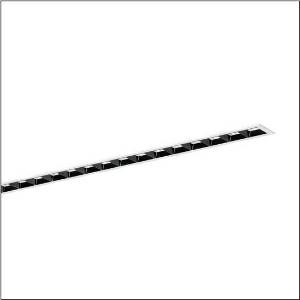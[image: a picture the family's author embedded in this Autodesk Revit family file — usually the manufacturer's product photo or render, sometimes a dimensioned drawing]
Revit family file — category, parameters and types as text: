
# Revit family: silica_r__21_51mx12tbt5w_1d14
name_source: partatom
category: Lighting Fixtures
units: mm (PartAtom-declared; Revit-internal decimal feet)

## family parameters
Cut with Voids When Loaded = No
Host = Face
Light Source = No
Part Type = Normal
Room Calculation Point = No
Round Connector Dimension = Use Diameter
Shared = No

## types (1)
- --- (1 x LED, 4650 lm, 40.2 W, 6500K)
    Apparent Load = 40 VA
    CIE Flux Codes = 84 100 100 100 100
    Color Rendering = 80
    Color Temperature = 6500K
    Default Elevation = 1800 mm
    Description = Silica® 21, office luminaire, primary light control with darklight reflector, of PMMA, black, CAT 2 (L<= 3000cd/m²), light emission: direct distribution, primary light characteristic: symmetric, installation type: recessed, LED, rated luminous flux: 4.650lm, luminous efficacy: 110lm/W, light colour: 8tw, colour temperature: 2700..6500K, with terminal, 3+2-pole, max. 2.5mm², mains connection: 220..240V, AC, 50/60Hz, rated input power: 42.2W, luminaire housing, of aluminium, traffic white (RAL 9016), length: 1.528mm, width: 79mm, height: 53mm, protection rating (complete): IP20, insulation class (complete): insulation class I (protective earthing), certification: CE, permissible operating ambient temperature: 0..+35°C, standard: EN 50419, packaging unit: 1 piece
    Height = 0 mm  [stored 0 ft]
    Lamp = 1 x LED
    Lamp Light Flux = 4650 lm
    Lamp Power = 40.2 W
    Lamp count = 1
    Length = 1527 mm
    Luminous efficacy = 116 lm/W
    Manufacturer = Siteco
    ModVariant = No
    Model = 51MX12TBT5W
    Mounting Place = Ceiling
    Mounting Type = Recessed
    Number of Poles = 1
    OnlyDefault = Yes
    Power Factor = 1
    Product Name = Silica® 21
    Product group = office luminaire | ceiling recessed
    ProductGroupID = 400
    Protection Class = Protection class I
    Protection Degree = IP 20
    RLX_Detail_Level = 1
    RlxData = <blob elided: 39209 chars, md5=d2da1403>
    Socket = socket
    Standby Power = 0 W
    System Light Flux = 4650 lm
    System Power = 40 W
    Type Comments = individual setting
    Type Image = l_1251632.jpg
    URL = http://relux.com
    VarID = @adj_046263
    Voltage = 0 V
    Weight = 0.00 kg
    Width = 79 mm

note: [stored X ft] marks values corroborated as IEEE doubles in the binary element streams (Revit-internal decimal feet)

## geometry (parser evidence)
native form markers: Blend x4, Sweep x11
no freeform markers — native parametric forms only
